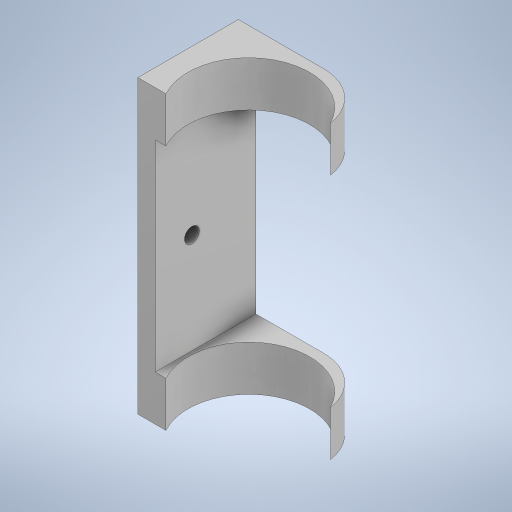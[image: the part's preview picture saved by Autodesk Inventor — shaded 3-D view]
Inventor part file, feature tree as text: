
AUTODESK INVENTOR PART (.ipt)
format: ipt  version: 2024 (Build 280153000, 153)  size: 312,320 bytes
history: native  units: in
note: dims shown in document units (in); Inventor stores cm internally (conversion verified against a paired STEP export)
features: extrude x6, sketch x6, plane x2, mirror x1
ambient origin geometry x8: Origin, YZ Plane, XZ Plane, XY Plane, X Axis, Y Axis, Z Axis, Center Point
bodies: Solid3 (feature_tree)
feature tree (15):
  plane  "Work Plane1"
  extrude  "Extrusion1"  Depth=0.2165in TaperAngle=0.0deg
  plane  "Work Plane4"
  extrude  "Extrusion2"  Depth=0.4085in TaperAngle=0.0deg
  mirror  "Mirror3"
  extrude  "Extrusion3"  Depth=0.2362in TaperAngle=0.0deg
  extrude  "Extrusion4"  Depth=0.0197in
  extrude  "Extrusion5"  [1 undecoded]
  extrude  "Extrusion6"  [1 undecoded]
  sketch  "Sketch2"  dims[d0=0.5906in d1=0.0in d2=0.2165in d3=0.0in]
  sketch  "Sketch3"  dims[d4=0.1181in d5=0.4085in d6=0.0in]
  sketch  "Sketch4"  dims[d7=0.0787in d8=0.0in d9=0.2362in d10=0.0in]
  sketch  "Sketch5"  dims[d11=0.2362in d12=0.0in d13=0.0197in]
  sketch  "Sketch7"  dims[d14=1.9685in]
  sketch  "Sketch8"
note: 2 required parameter values undecoded (feature->parameter linkage not recoverable at this tier; creation-order binding heuristic only, values carry confidence <= 0.55)
